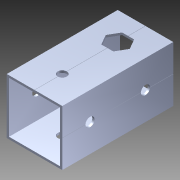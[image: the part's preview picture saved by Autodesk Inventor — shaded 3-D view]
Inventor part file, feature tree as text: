
AUTODESK INVENTOR PART (.ipt)
format: ipt  version: 2014 (Build 180170000, 170)  size: 1,168,896 bytes
history: native  units: in
note: dims shown in document units (in); Inventor stores cm internally (conversion verified against a paired STEP export)
features: extrude x2, sketch x2, pattern_circular x1, other x1, plane x1, imported_body x1
ambient origin geometry x8: Origin, YZ Plane, XZ Plane, XY Plane, X Axis, Y Axis, Z Axis, Center Point
bodies: Body1 (feature_tree)
feature tree (8):
  pattern_circular  "CirPattern2"
  other  "217-3426-STEP1"
  plane  "Work Plane1"
  extrude  "Extrusion1"  Depth=3937.0079in TaperAngle=0.0deg
  extrude  "Extrusion2"  Depth=2.0in TaperAngle=0.0deg
  imported_body  "Base1"
  sketch  "Sketch1"  dims[d0=-2.0in d1=3937.0079in d2=0.0in]
  sketch  "Sketch3"  dims[d3=0.375in d4=2.0in d5=0.0in]
